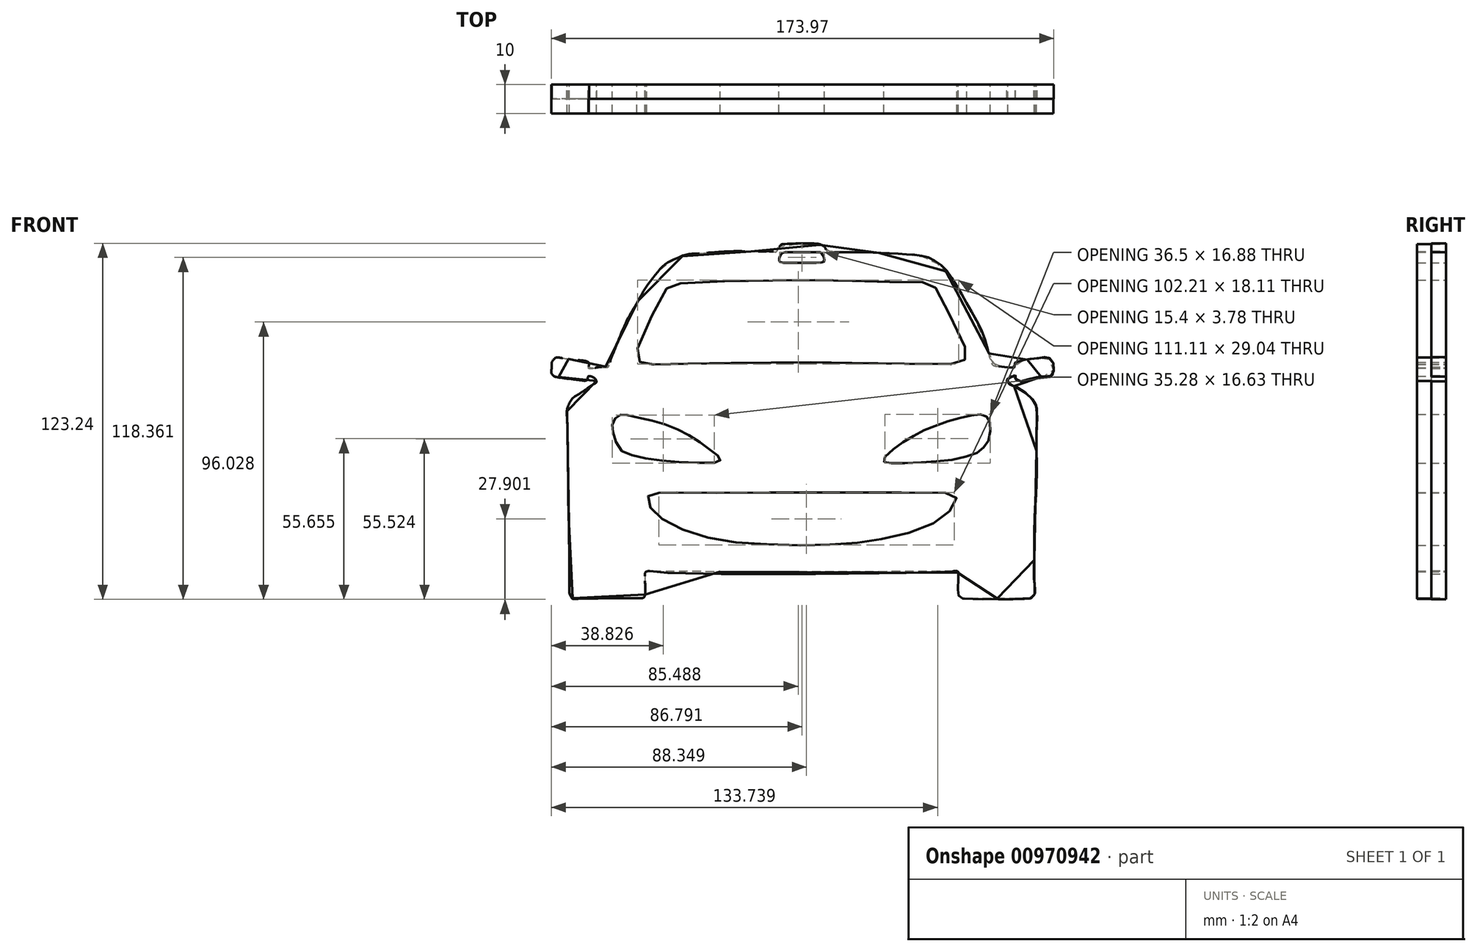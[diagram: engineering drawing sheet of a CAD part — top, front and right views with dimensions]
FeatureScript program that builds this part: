
annotation { "Feature Type Name" : "Feature", "Feature Type Description" : "" }
export const myFeature = defineFeature(function(context is Context, id is Id, definition is map)
    precondition{}
    {
        {
            var Q0;
            Q0=qCreatedBy(makeId("Front.planeOp"),FACE);
            var sketch = newSketch(context, id + "F0", { "sketchPlane" : qUnion([Q0])});
            skFitSpline(sketch, "E0", {"points": [v(-21.27, 56.96) * mm, v(-13.6, 56.91) * mm, v(-12.5, 57.15) * mm, v(-11.15, 58.8) * mm, v(-9.8, 59.33) * mm, v(2.4, 59.33) * mm, v(3.34, 59.13) * mm, v(3.88, 58.78) * mm, v(5.1, 57.11) * mm, v(5.85, 56.82) * mm, v(14.75, 56.72) * mm, v(22.63, 56.52) * mm, v(29.76, 56.13) * mm, v(36.44, 55.52) * mm, v(40.67, 54.33) * mm, v(45.3, 50.99) * mm, v(50.02, 44.69) * mm, v(55.14, 35.73) * mm, v(59.96, 25) * mm, v(62.62, 18.01) * mm, v(63.7, 17.32) * mm, v(66.95, 16.93) * mm, v(69.51, 16.93) * mm, v(69.9, 17.62) * mm, v(70.46, 18.33) * mm, v(74.6, 19.5) * mm, v(79.36, 20.18) * mm, v(81.13, 20.18) * mm, v(82.7, 19) * mm, v(83.4, 16.44) * mm, v(82.7, 14.47) * mm, v(79.55, 13.58) * mm, v(73.65, 12.4) * mm, v(71.38, 12.3) * mm, v(70.4, 13.1) * mm, v(70.1, 13.68) * mm, v(68.23, 13.19) * mm, v(67.68, 12) * mm, v(69.45, 10.53) * mm, v(73.48, 8.02) * mm, v(76.24, 5.46) * mm, v(77.17, 3.44) * mm, v(77.57, -6.1) * mm, v(77.52, -20.57) * mm, v(76.98, -36) * mm, v(76.78, -48.98) * mm, v(76.88, -57.55) * mm, v(76.98, -61) * mm, v(76.62, -61.97) * mm, v(75.84, -62.78) * mm, v(74.34, -63.08) * mm, v(52.48, -63.08) * mm, v(51.6, -62.88) * mm, v(50.87, -62.32) * mm, v(50.52, -61.72) * mm, v(50.4, -60.34) * mm, v(50.5, -55.86) * mm, v(50.47, -54.56) * mm, v(50.15, -53.9) * mm, v(49.14, -53.72) * mm, v(47.86, -53.75) * mm, v(-54.07, -53.72) * mm, v(-56.97, -53.7) * mm, v(-57.74, -54.05) * mm, v(-57.95, -54.76) * mm, v(-57.95, -55.97) * mm, v(-57.84, -61.33) * mm, v(-57.95, -61.92) * mm, v(-58.47, -62.65) * mm, v(-59.62, -62.97) * mm, v(-61.43, -63) * mm, v(-81.16, -63.24) * mm, v(-82.07, -63.28) * mm, v(-82.94, -63.07) * mm, v(-83.53, -62.48) * mm, v(-83.95, -61.5) * mm, v(-84.08, -59.94) * mm, v(-84.08, -54.86) * mm, v(-84.22, -40.34) * mm, v(-84.5, -23.74) * mm, v(-84.78, -3.56) * mm, v(-84.85, 1.76) * mm, v(-84.54, 3.2) * mm, v(-83.42, 5.38) * mm, v(-81.86, 6.92) * mm, v(-79, 8.8) * mm, v(-76.4, 10.57) * mm, v(-74.76, 11.68) * mm, v(-74.69, 12.1) * mm, v(-75.1, 12.83) * mm, v(-76.08, 13.53) * mm, v(-77.05, 13.8) * mm, v(-77.5, 13.77) * mm, v(-77.75, 13.14) * mm, v(-77.96, 12.62) * mm, v(-78.55, 12.3) * mm, v(-79.77, 12.34) * mm, v(-87.7, 13.5) * mm, v(-89.72, 14.3) * mm, v(-90.24, 15.3) * mm, v(-90.24, 16.7) * mm, v(-90.1, 18.33) * mm, v(-89.65, 19.3) * mm, v(-88.68, 20.07) * mm, v(-87.18, 20.14) * mm, v(-84.36, 19.8) * mm, v(-80.57, 19.3) * mm, v(-78.03, 18.82) * mm, v(-77.5, 18.33) * mm, v(-77.44, 17.29) * mm, v(-77.44, 16.8) * mm, v(-76.25, 16.59) * mm, v(-73.54, 16.87) * mm, v(-70.9, 17.32) * mm, v(-70.13, 18.5) * mm, v(-68.67, 22.23) * mm, v(-64.14, 32.67) * mm, v(-60.73, 39.1) * mm, v(-57.74, 44.15) * mm, v(-54.17, 48.98) * mm, v(-50.87, 52.32) * mm, v(-47.47, 54.3) * mm, v(-43.78, 55.67) * mm, v(-39.94, 56.21) * mm, v(-32.32, 56.75) * mm, v(-25.23, 57) * mm, v(-21.27, 56.96) * mm]});
            skFitSpline(sketch, "E1", {"points": [v(-69.2, -3.04) * mm, v(-68.67, -1.37) * mm, v(-67.34, 0) * mm, v(-65.87, 0.56) * mm, v(-64.2, 0.33) * mm, v(-62.97, 0) * mm, v(-60.87, -0.44) * mm, v(-58, -1.06) * mm, v(-52.95, -2.23) * mm, v(-46.23, -4.8) * mm, v(-41.02, -7.6) * mm, v(-35.75, -11.35) * mm, v(-33, -13.52) * mm, v(-31.94, -14.63) * mm, v(-31.94, -15.5) * mm, v(-32.94, -16.1) * mm, v(-42.74, -16.03) * mm, v(-53.73, -15.24) * mm, v(-62.32, -13.58) * mm, v(-66.12, -11.94) * mm, v(-68.35, -7.96) * mm, v(-69.11, -4.62) * mm, v(-69.2, -3.04) * mm]});
            skFitSpline(sketch, "E2", {"points": [v(25.1, -14.17) * mm, v(28.14, -11.45) * mm, v(31.48, -8.98) * mm, v(35.34, -6.68) * mm, v(39.27, -4.6) * mm, v(43.14, -3.2) * mm, v(48.5, -1.29) * mm, v(52.53, -0.42) * mm, v(56.36, 0.52) * mm, v(58.48, 0.59) * mm, v(59.81, 0.17) * mm, v(60.77, -0.78) * mm, v(61.41, -1.9) * mm, v(61.6, -3.62) * mm, v(61.32, -6.93) * mm, v(60.65, -9.01) * mm, v(59.48, -10.65) * mm, v(58.04, -12.2) * mm, v(55.03, -13.4) * mm, v(49.65, -14.9) * mm, v(42.33, -15.71) * mm, v(35.22, -16.18) * mm, v(28.05, -16.3) * mm, v(25.85, -16.24) * mm, v(24.8, -15.77) * mm, v(24.71, -15.04) * mm, v(25.1, -14.17) * mm]});
            skFitSpline(sketch, "E3", {"points": [v(-53.14, -26.6) * mm, v(-54.77, -26.65) * mm, v(-56.01, -27.05) * mm, v(-57.16, -28.1) * mm, v(-57.2, -29.59) * mm, v(-56.19, -31.5) * mm, v(-54.66, -33.14) * mm, v(-51.87, -35.68) * mm, v(-46.55, -38.57) * mm, v(-40.39, -40.93) * mm, v(-30.78, -43.16) * mm, v(-22.26, -44) * mm, v(-9.41, -44.73) * mm, v(1.4, -44.66) * mm, v(11.01, -44.24) * mm, v(18.64, -43.5) * mm, v(25.1, -42.4) * mm, v(34.02, -40.2) * mm, v(41.43, -37.35) * mm, v(45.15, -35.16) * mm, v(48.74, -31.36) * mm, v(49.89, -29.38) * mm, v(49.75, -27.95) * mm, v(48.8, -26.94) * mm, v(46.9, -26.6) * mm, v(24.93, -26.53) * mm, v(8.72, -26.46) * mm, v(-18.5, -26.53) * mm, v(-44.32, -26.53) * mm, v(-51.07, -26.55) * mm, v(-53.14, -26.6) * mm]});
            skFitSpline(sketch, "E4", {"points": [v(-60.45, 23.47) * mm, v(-54.81, 36.2) * mm, v(-50.36, 44.28) * mm, v(-49.6, 45.25) * mm, v(-47.43, 45.8) * mm, v(-28.43, 46.71) * mm, v(-5.81, 47.06) * mm, v(10.55, 46.92) * mm, v(25.37, 46.5) * mm, v(37.76, 46.3) * mm, v(41.3, 45.8) * mm, v(42.35, 44.83) * mm, v(44.3, 41.28) * mm, v(51.68, 26.39) * mm, v(53.35, 22.07) * mm, v(53.35, 20.68) * mm, v(52.59, 19.36) * mm, v(51.2, 18.38) * mm, v(47.78, 18.04) * mm, v(21.4, 18.25) * mm, v(0.8, 18.6) * mm, v(-15.97, 18.45) * mm, v(-33.8, 18.25) * mm, v(-51.68, 17.9) * mm, v(-57.46, 17.83) * mm, v(-58.92, 18.1) * mm, v(-60.1, 19.29) * mm, v(-60.66, 21.38) * mm, v(-60.45, 23.47) * mm]});
            skFitSpline(sketch, "E5", {"points": [v(-11.3, 55.13) * mm, v(-10.6, 56.3) * mm, v(-9.53, 56.68) * mm, v(1.76, 56.74) * mm, v(3.02, 56.59) * mm, v(3.52, 55.9) * mm, v(4.13, 54.02) * mm, v(3.78, 53.37) * mm, v(2.35, 53.11) * mm, v(-10.17, 53.1) * mm, v(-11.4, 53.5) * mm, v(-11.54, 54.27) * mm, v(-11.3, 55.13) * mm]});
            skSolve(sketch);
        }
        {
            var Q0;
            Q0 = qSketchRegion(id + "F0", true);
            extrude(context, id + "F1", {"entities" : qUnion([Q0]), "depth" : 10 * mm, "offsetDistance" : 25 * mm});
        }
        {
            var Q0;
            Q0=qCreatedBy(makeId("Front.planeOp"),FACE);
            var sketch = newSketch(context, id + "F2", { "sketchPlane" : qUnion([Q0])});
            skFitSpline(sketch, "E6.0", {"points": [v(-21.27, 56.96) * mm, v(-18.93, 56.94) * mm, v(-13.62, 56.94) * mm, v(-12.48, 56.88) * mm, v(-11.08, 59.06) * mm, v(-10.04, 59.52) * mm, v(2.43, 59.52) * mm, v(3.28, 59.15) * mm, v(3.98, 58.89) * mm, v(5.1, 56.93) * mm, v(5.9, 56.72) * mm, v(15.42, 56.76) * mm, v(22.42, 56.56) * mm, v(29.66, 56.15) * mm, v(36.41, 55.67) * mm, v(40.8, 54.62) * mm, v(45.74, 51.11) * mm, v(50.24, 44.59) * mm, v(55.32, 35.71) * mm, v(59.98, 25.78) * mm, v(62.23, 17.88) * mm, v(63.69, 17.22) * mm, v(66.85, 16.98) * mm, v(69.65, 16.57) * mm, v(69.88, 17.67) * mm, v(70.4, 18.6) * mm, v(74.71, 19.64) * mm, v(79.24, 20.16) * mm, v(81.13, 20.4) * mm, v(82.99, 19.12) * mm, v(83.6, 16.47) * mm, v(82.97, 14) * mm, v(79.43, 13.68) * mm, v(73.78, 12.38) * mm, v(71.46, 12.03) * mm, v(70.27, 12.99) * mm, v(70.32, 14) * mm, v(68.02, 13.4) * mm, v(67.28, 11.81) * mm, v(69.65, 10.4) * mm, v(73.53, 8.23) * mm, v(76.37, 5.51) * mm, v(77.55, 3.35) * mm, v(77.55, -6.93) * mm, v(77.67, -20.57) * mm, v(76.88, -35.82) * mm, v(76.76, -48.55) * mm, v(76.77, -57.11) * mm, v(77.12, -60.92) * mm, v(76.72, -61.97) * mm, v(75.72, -62.96) * mm, v(74.57, -63.22) * mm, v(52.31, -63.26) * mm, v(51.72, -62.96) * mm, v(50.8, -62.35) * mm, v(50.45, -61.67) * mm, v(50.36, -60.31) * mm, v(50.5, -55.87) * mm, v(50.52, -54.65) * mm, v(50.3, -53.73) * mm, v(48.87, -53.72) * mm, v(48.48, -53.83) * mm, v(-54.8, -54.02) * mm, v(-56.62, -53.58) * mm, v(-57.87, -53.95) * mm, v(-57.97, -54.87) * mm, v(-57.96, -55.87) * mm, v(-57.78, -61.37) * mm, v(-57.9, -61.87) * mm, v(-58.38, -62.83) * mm, v(-59.85, -63) * mm, v(-61.12, -62.98) * mm, v(-81.3, -63.15) * mm, v(-81.93, -63.32) * mm, v(-83.02, -63.15) * mm, v(-83.57, -62.5) * mm, v(-84.04, -61.46) * mm, v(-84.11, -59.7) * mm, v(-84.05, -54.32) * mm, v(-84.2, -39.5) * mm, v(-84.54, -24.48) * mm, v(-84.68, -4.3) * mm, v(-84.97, 1.6) * mm, v(-84.61, 3.17) * mm, v(-83.5, 5.55) * mm, v(-81.9, 6.99) * mm, v(-78.93, 8.77) * mm, v(-76.61, 10.52) * mm, v(-74.66, 11.56) * mm, v(-74.64, 12.12) * mm, v(-75.07, 12.91) * mm, v(-76.03, 13.6) * mm, v(-77.01, 13.8) * mm, v(-77.59, 13.9) * mm, v(-77.76, 13.12) * mm, v(-77.88, 12.57) * mm, v(-78.65, 12.22) * mm, v(-79.81, 12.34) * mm, v(-87.75, 13.33) * mm, v(-89.74, 14.07) * mm, v(-90.37, 15.31) * mm, v(-90.22, 16.69) * mm, v(-90.2, 18.35) * mm, v(-89.73, 19.33) * mm, v(-88.7, 20.26) * mm, v(-87.09, 20.15) * mm, v(-84.29, 19.78) * mm, v(-80.73, 19.33) * mm, v(-78.05, 18.96) * mm, v(-77.4, 18.4) * mm, v(-77.39, 17.3) * mm, v(-77.62, 16.66) * mm, v(-76.04, 16.5) * mm, v(-73.64, 16.94) * mm, v(-70.69, 17) * mm, v(-70.07, 18.69) * mm, v(-68.6, 22.5) * mm, v(-64.26, 32.87) * mm, v(-60.82, 38.94) * mm, v(-57.87, 44.19) * mm, v(-54.29, 48.98) * mm, v(-51.06, 52.48) * mm, v(-47.54, 54.34) * mm, v(-43.73, 55.87) * mm, v(-39.83, 56.24) * mm, v(-32.39, 56.8) * mm, v(-25.1, 57.05) * mm, v(-22.96, 56.98) * mm, v(-21.27, 56.96) * mm]});
            skSolve(sketch);
        }
        {
            var Q0;
            Q0 = qSketchRegion(id + "F2", true);
            extrude(context, id + "F3", {"entities" : qUnion([Q0]), "depth" : 5 * mm, "offsetDistance" : 25 * mm});
        }
    });
